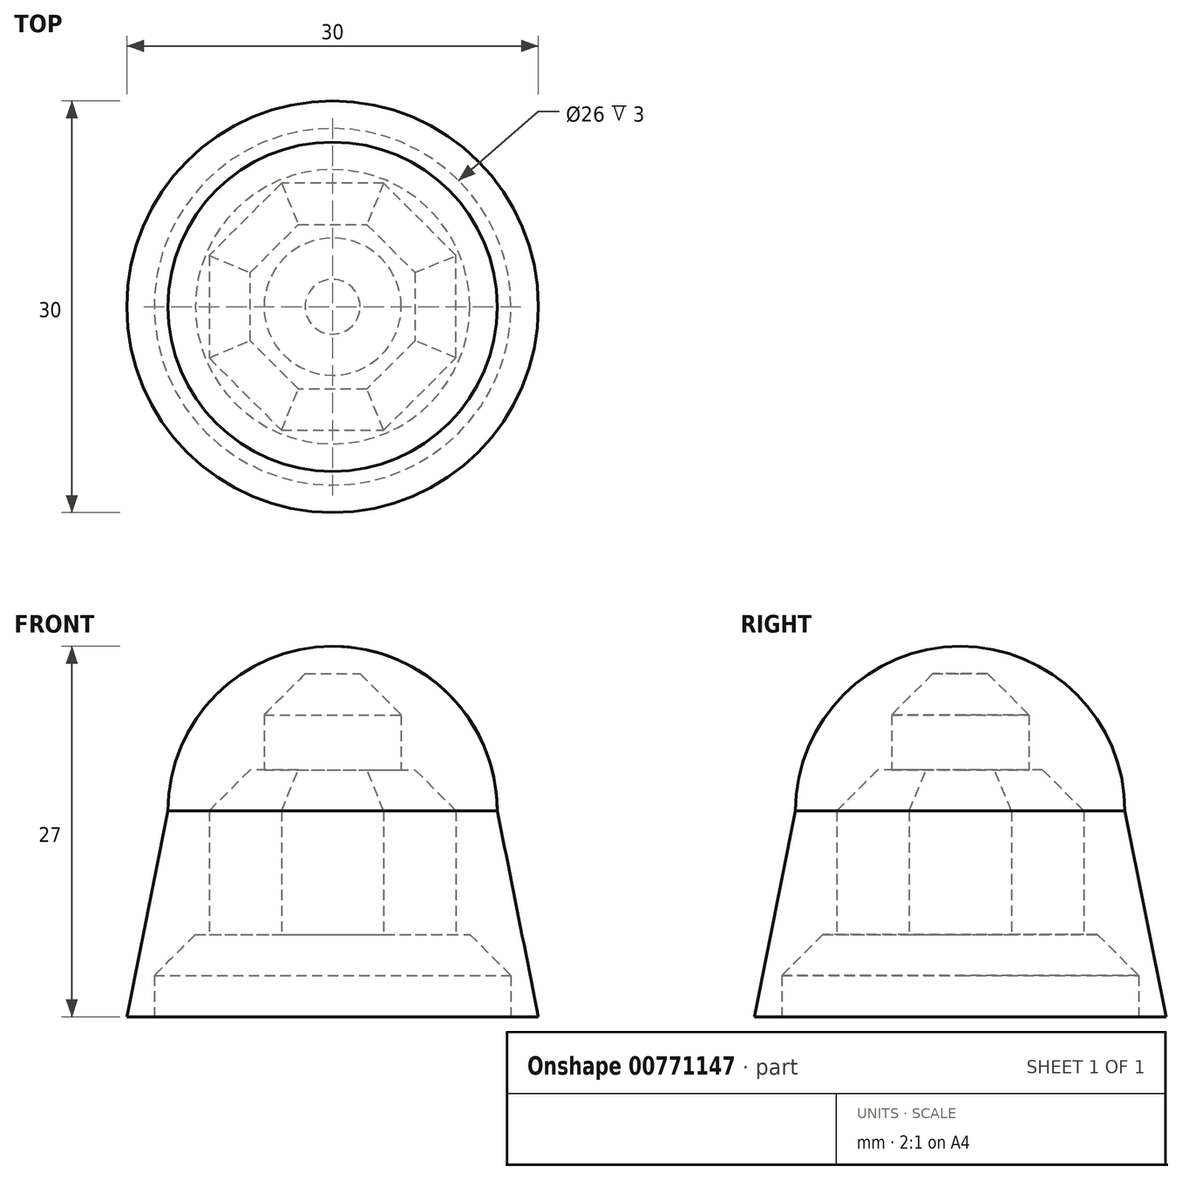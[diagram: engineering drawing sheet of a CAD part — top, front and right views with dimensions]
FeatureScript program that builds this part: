
annotation { "Feature Type Name" : "Feature", "Feature Type Description" : "" }
export const myFeature = defineFeature(function(context is Context, id is Id, definition is map)
    precondition{}
    {
        {
            var Q0;
            Q0=qCreatedBy(makeId("Front.planeOp"),FACE);
            var sketch = newSketch(context, id + "F0", { "sketchPlane" : qUnion([Q0])});
            skLineSegment(sketch, "E0", {"start": v(0, 0) * mm, "end": v(15, 0) * mm});
            skLineSegment(sketch, "E1", {"start": v(24.33, 15) * mm, "end": v(-7.04, 15) * mm, "construction": true});
            skArc(sketch, "E2", {"start": v(12, 15) * mm, "mid": v(8.49, 23.49) * mm, "end": v(0, 27) * mm});
            skLineSegment(sketch, "E3", {"start": v(0, 48.34) * mm, "end": v(0, 27) * mm, "construction": true});
            skPoint(sketch, "E4.start.orphan", {"position": v(-10, 0) * mm});
            skLineSegment(sketch, "E5", {"start": v(0, 27) * mm, "end": v(0, 0) * mm});
            skLineSegment(sketch, "E6", {"start": v(15, 0) * mm, "end": v(12, 15) * mm});
            skSolve(sketch);
        }
        {
            var Q0;
            Q0=makeQuery(id+"F0.imprint","IMPRINT",FACE,{"disambiguationData":[TD([[makeQuery(id+"F0.imprint","IMPRINT",EDGE,{"derivedFrom":sQuery(id+"F0.wireOp",EDGE,"E0")}),1.0]])]});
            var Q1;
            Q1=sQuery(id+"F0.wireOp",EDGE,"E5");
            revolve(context, id + "F1", {"surfaceOperationType" : NewSurfaceOperationType.NEW, "entities" : qUnion([Q0]), "axis" : qUnion([Q1]), "revolveType" : RevolveType.FULL});
        }
        {
            var Q0;
            Q0=makeQuery(id+"F1.opRevolve","SWEPT_FACE",FACE,{"disambiguationData":[OSD([sQuery(id+"F0.wireOp",EDGE,"E0")])]});
            var sketch = newSketch(context, id + "F2", { "sketchPlane" : qUnion([Q0])});
            skCircle(sketch, "E7", {"center": v(0, 0) * mm, "radius": 5 * mm});
            skCircle(sketch, "E8", {"center": v(0, 0) * mm, "radius": 4.79 * mm});
            skCircle(sketch, "E9", {"center": v(0, 0) * mm, "radius": 13 * mm});
            skCircle(sketch, "E10.cCircle", {"center": v(0, 0) * mm, "radius": 9 * mm, "construction": true});
            skLineSegment(sketch, "E10.0", {"start": v(9, 3.73) * mm, "end": v(9, -3.73) * mm});
            skLineSegment(sketch, "E10.1", {"start": v(9, -3.73) * mm, "end": v(3.73, -9) * mm});
            skLineSegment(sketch, "E10.2", {"start": v(3.73, -9) * mm, "end": v(-3.73, -9) * mm});
            skLineSegment(sketch, "E10.3", {"start": v(-3.73, -9) * mm, "end": v(-9, -3.73) * mm});
            skLineSegment(sketch, "E10.4", {"start": v(-9, -3.73) * mm, "end": v(-9, 3.73) * mm});
            skLineSegment(sketch, "E10.5", {"start": v(-9, 3.73) * mm, "end": v(-3.73, 9) * mm});
            skLineSegment(sketch, "E10.6", {"start": v(-3.73, 9) * mm, "end": v(3.73, 9) * mm});
            skLineSegment(sketch, "E10.7", {"start": v(3.73, 9) * mm, "end": v(9, 3.73) * mm});
            skPoint(sketch, "E10.0.midPoint", {"position": v(9, 0) * mm});
            skSolve(sketch);
        }
        {
            var Q0;
            Q0=makeQuery(id+"F2.imprint","IMPRINT",FACE,{"disambiguationData":[TD([[makeQuery(id+"F2.imprint","IMPRINT",EDGE,{"derivedFrom":sQuery(id+"F2.wireOp",EDGE,"E8")}),1.0]])]});
            var Q1;
            Q1=makeQuery(id+"F2.imprint","IMPRINT",FACE,{"disambiguationData":[TD([[makeQuery(id+"F2.imprint","IMPRINT",EDGE,{"derivedFrom":sQuery(id+"F2.wireOp",EDGE,"E7")}),1.0]])]});
            extrude(context, id + "F3", {"entities" : qUnion([Q0, Q1]), "operationType" : NewBodyOperationType.REMOVE, "oppositeDirection" : true, "depth" : 25 * mm, "offsetDistance" : 25 * mm});
        }
        {
            var Q0;
            Q0=makeQuery(id+"F2.imprint","IMPRINT",FACE,{"disambiguationData":[TD([[makeQuery(id+"F2.imprint","IMPRINT",EDGE,{"derivedFrom":sQuery(id+"F2.wireOp",EDGE,"E7")}),-1.0]])]});
            extrude(context, id + "F4", {"entities" : qUnion([Q0]), "operationType" : NewBodyOperationType.REMOVE, "oppositeDirection" : true, "depth" : 18 * mm, "offsetDistance" : 25 * mm});
        }
        {
            var Q0;
            Q0=makeQuery(id+"F2.imprint","IMPRINT",FACE,{"disambiguationData":[TD([[makeQuery(id+"F2.imprint","IMPRINT",EDGE,{"derivedFrom":sQuery(id+"F2.wireOp",EDGE,"E9")}),1.0]])]});
            extrude(context, id + "F5", {"entities" : qUnion([Q0]), "operationType" : NewBodyOperationType.REMOVE, "oppositeDirection" : true, "depth" : 6 * mm, "offsetDistance" : 25 * mm});
        }
        {
            var Q0;
            Q0=makeQuery(id+"F3.boolean.opBoolean","COPY",EDGE,{"derivedFrom":makeQuery(id+"F3.opExtrude","CAP_EDGE",EDGE,{"disambiguationData":[OSD([sQuery(id+"F2.wireOp",EDGE,"E7")])],"isStart":false})});
            var Q1;
            Q1=makeQuery(id+"F4.boolean.opBoolean","COPY",EDGE,{"derivedFrom":makeQuery(id+"F4.opExtrude","CAP_EDGE",EDGE,{"disambiguationData":[OSD([sQuery(id+"F2.wireOp",EDGE,"bc77e31f-ddaa-47ac-b1f8-d8747e7a2e9b.1")])],"isStart":false})});
            var Q2;
            Q2=makeQuery(id+"F4.boolean.opBoolean","COPY",EDGE,{"derivedFrom":makeQuery(id+"F4.opExtrude","CAP_EDGE",EDGE,{"disambiguationData":[OSD([sQuery(id+"F2.wireOp",EDGE,"bc77e31f-ddaa-47ac-b1f8-d8747e7a2e9b.0")])],"isStart":false})});
            var Q3;
            Q3=makeQuery(id+"F4.boolean.opBoolean","COPY",EDGE,{"derivedFrom":makeQuery(id+"F4.opExtrude","CAP_EDGE",EDGE,{"disambiguationData":[OSD([sQuery(id+"F2.wireOp",EDGE,"bc77e31f-ddaa-47ac-b1f8-d8747e7a2e9b.4")])],"isStart":false})});
            var Q4;
            Q4=makeQuery(id+"F4.boolean.opBoolean","COPY",EDGE,{"derivedFrom":makeQuery(id+"F4.opExtrude","CAP_EDGE",EDGE,{"disambiguationData":[OSD([sQuery(id+"F2.wireOp",EDGE,"bc77e31f-ddaa-47ac-b1f8-d8747e7a2e9b.3")])],"isStart":false})});
            var Q5;
            Q5=makeQuery(id+"F4.boolean.opBoolean","COPY",EDGE,{"derivedFrom":makeQuery(id+"F4.opExtrude","CAP_EDGE",EDGE,{"disambiguationData":[OSD([sQuery(id+"F2.wireOp",EDGE,"bc77e31f-ddaa-47ac-b1f8-d8747e7a2e9b.2")])],"isStart":false})});
            var Q6;
            Q6=makeQuery(id+"F5.boolean.opBoolean","COPY",EDGE,{"derivedFrom":makeQuery(id+"F5.opExtrude","CAP_EDGE",EDGE,{"disambiguationData":[OSD([sQuery(id+"F2.wireOp",EDGE,"E9")])],"isStart":false})});
            var Q7;
            Q7=makeQuery(id+"F4.boolean.opBoolean","COPY",EDGE,{"derivedFrom":makeQuery(id+"F4.opExtrude","CAP_EDGE",EDGE,{"disambiguationData":[OSD([sQuery(id+"F2.wireOp",EDGE,"E10.2")])],"isStart":false})});
            var Q8;
            Q8=makeQuery(id+"F4.boolean.opBoolean","COPY",EDGE,{"derivedFrom":makeQuery(id+"F4.opExtrude","CAP_EDGE",EDGE,{"disambiguationData":[OSD([sQuery(id+"F2.wireOp",EDGE,"E10.1")])],"isStart":false})});
            var Q9;
            Q9=makeQuery(id+"F4.boolean.opBoolean","COPY",EDGE,{"derivedFrom":makeQuery(id+"F4.opExtrude","CAP_EDGE",EDGE,{"disambiguationData":[OSD([sQuery(id+"F2.wireOp",EDGE,"E10.0")])],"isStart":false})});
            var Q10;
            Q10=makeQuery(id+"F4.boolean.opBoolean","COPY",EDGE,{"derivedFrom":makeQuery(id+"F4.opExtrude","CAP_EDGE",EDGE,{"disambiguationData":[OSD([sQuery(id+"F2.wireOp",EDGE,"E10.3")])],"isStart":false})});
            var Q11;
            Q11=makeQuery(id+"F4.boolean.opBoolean","COPY",EDGE,{"derivedFrom":makeQuery(id+"F4.opExtrude","CAP_EDGE",EDGE,{"disambiguationData":[OSD([sQuery(id+"F2.wireOp",EDGE,"E10.4")])],"isStart":false})});
            var Q12;
            Q12=makeQuery(id+"F4.boolean.opBoolean","COPY",EDGE,{"derivedFrom":makeQuery(id+"F4.opExtrude","CAP_EDGE",EDGE,{"disambiguationData":[OSD([sQuery(id+"F2.wireOp",EDGE,"E10.5")])],"isStart":false})});
            var Q13;
            Q13=makeQuery(id+"F4.boolean.opBoolean","COPY",EDGE,{"derivedFrom":makeQuery(id+"F4.opExtrude","CAP_EDGE",EDGE,{"disambiguationData":[OSD([sQuery(id+"F2.wireOp",EDGE,"E10.6")])],"isStart":false})});
            var Q14;
            Q14=makeQuery(id+"F4.boolean.opBoolean","COPY",EDGE,{"derivedFrom":makeQuery(id+"F4.opExtrude","CAP_EDGE",EDGE,{"disambiguationData":[OSD([sQuery(id+"F2.wireOp",EDGE,"E10.7")])],"isStart":false})});
            chamfer(context, id + "F6", {"entities" : qUnion([Q0, Q1, Q2, Q3, Q4, Q5, Q6, Q7, Q8, Q9, Q10, Q11, Q12, Q13, Q14]), "width" : 3 * mm, "tangentPropagation" : true});
        }
    });
